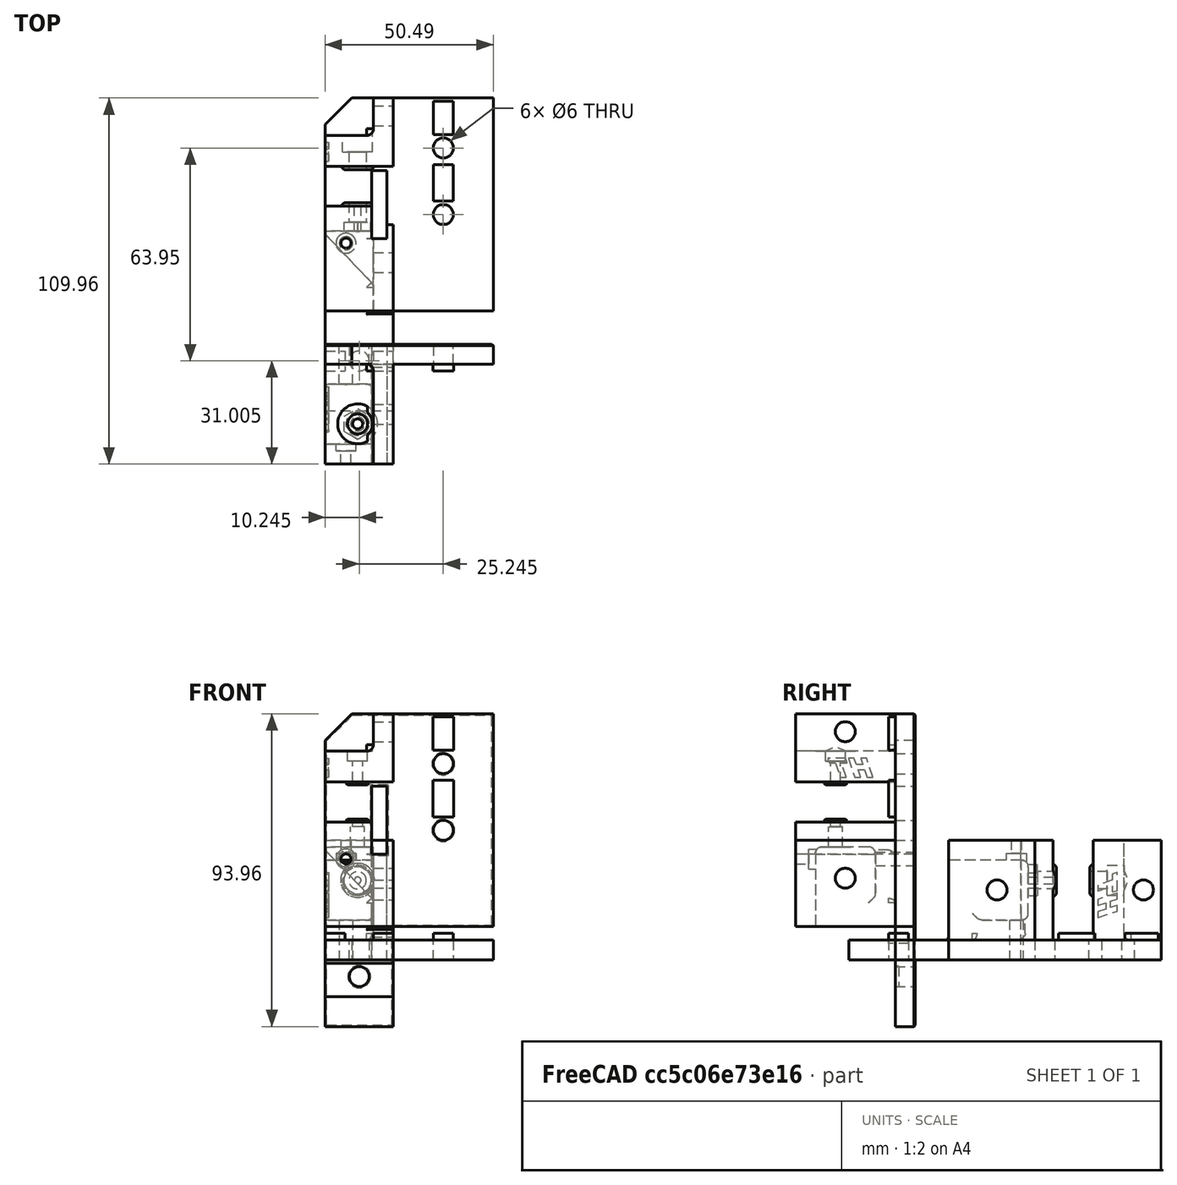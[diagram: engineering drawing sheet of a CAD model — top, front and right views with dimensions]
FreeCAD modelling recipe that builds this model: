
FCSTD DOCUMENT  (FreeCAD 0.18R16146 (Git))
Label: rear-idler-right-2
License: All rights reserved
LicenseURL: http://en.wikipedia.org/wiki/All_rights_reserved
objects: Part::Box×11, Part::Cylinder×11, Part::Cut×10, Part::MultiFuse×7, Part::Feature×5, Part::Chamfer×3
note: 47 computed .brp shape members not serialized (recipe doc carries the construction recipe); baked Part::Feature solids carry a one-line shape summary decoded from their .brp

FEATURE [Part::Feature] Part__Feature  label="PulleyMount_REAR_RIGHT_Body"
  Placement = pos=(-422.5,-448.82,-414) rot=(0,-1,0;1.5708rad)
  shape: bbox 51.93 x 93.95 x 36 mm, 87 faces (baked)
FEATURE [Part::Feature] Part__Feature001  label="PulleyMount_REAR_RIGHT_Body001"
  shape: bbox 51.93 x 93.95 x 36 mm, 87 faces (baked)
FEATURE [Part::Box] Box  label="Cube"
  AttacherType = Attacher::AttachEngine3D
  Height = 3
  Length = 6
  Placement = pos=(12,43,5) rot=(0,0,1;0rad)
  Width = 11
FEATURE [Part::Box] Box001  label="Cube001"
  AttacherType = Attacher::AttachEngine3D
  Height = 3
  Length = 6
  Placement = pos=(12,63,5) rot=(0,0,1;0rad)
  Width = 10
FEATURE [Part::Box] Box002  label="Cube002"
  AttacherType = Attacher::AttachEngine3D
  Height = 3
  Length = 6
  Placement = pos=(-20.49,-8,5) rot=(0,0,1;0rad)
  Width = 6
FEATURE [Part::Box] Box003  label="Cube003"
  AttacherType = Attacher::AttachEngine3D
  Height = 3
  Length = 6
  Placement = pos=(-6,-8,5) rot=(0,0,1;0rad)
  Width = 6
FEATURE [Part::Box] Box004  label="Cube004"
  AttacherType = Attacher::AttachEngine3D
  Height = 3
  Length = 13
  Placement = pos=(-12,4,6.01) rot=(0,0,1;0rad)
  Width = 6
FEATURE [Part::Cut] Cut
  Base = -> Part__Feature001
  Tool = -> Box004
FEATURE [Part::MultiFuse] Fusion
  Shapes = -> [Box003,Box002,Box001,Box,Cut]
FEATURE [Part::Feature] Fusion001
  shape: bbox 51.93 x 93.95 x 36 mm, 110 faces (baked)
FEATURE [Part::Chamfer] Chamfer
  Base = -> Fusion001
  Edges = 15 edges r=0.4: [Edge27,Edge29,Edge30,Edge31,Edge32,Edge33,Edge34,Edge35,Edge36,Edge37,Edge38,Edge39,Edge40,Edge41,Edge42]
FEATURE [Part::Cylinder] Cylinder  label="pos"
  Angle = 360
  AttacherType = Attacher::AttachEngine3D
  Height = 7.5
  Placement = pos=(-10.74,33.96,23.92) rot=(-1,0,0;1.5708rad)
  Radius = 1
FEATURE [Part::Cylinder] Cylinder001  label="pos001"
  Angle = 360
  AttacherType = Attacher::AttachEngine3D
  Height = 7.5
  Placement = pos=(-10.74,33.96,23.92) rot=(-1,0,0;1.5708rad)
  Radius = 6
FEATURE [Part::Box] Box005  label="Cube005"
  AttacherType = Attacher::AttachEngine3D
  Height = 17
  Length = 10
  Placement = pos=(-6.5,33,16) rot=(0,0,1;0rad)
  Width = 23
FEATURE [Part::Cut] Cut001
  Base = -> Cylinder001
  Tool = -> Box005
FEATURE [Part::MultiFuse] Fusion002
  Shapes = -> [Chamfer,Cut001]
FEATURE [Part::Cylinder] Cylinder002  label="pos002"
  Angle = 360
  AttacherType = Attacher::AttachEngine3D
  Height = 9.25
  Placement = pos=(-10.74,53.46,23.92) rot=(-1,0,0;1.5708rad)
  Radius = 6
FEATURE [Part::MultiFuse] Fusion003
  Shapes = -> [Cylinder002,Fusion002]
FEATURE [Part::Cylinder] Cylinder003  label="pos003"
  Angle = 360
  AttacherType = Attacher::AttachEngine3D
  Height = 3
  Placement = pos=(-10.74,50.46,23.92) rot=(-1,0,0;1.5708rad)
  Radius = 6
FEATURE [Part::Cylinder] Cylinder004  label="pos004"
  Angle = 360
  AttacherType = Attacher::AttachEngine3D
  Height = 3
  Placement = pos=(-10.74,41.46,23.92) rot=(-1,0,0;1.5708rad)
  Radius = 6
FEATURE [Part::Cut] Cut002
  Base = -> Fusion003
  Tool = -> Cylinder004
FEATURE [Part::Cut] Cut003
  Base = -> Cut002
  Tool = -> Cylinder003
FEATURE [Part::Cylinder] Cylinder005  label="pos005"
  Angle = 360
  AttacherType = Attacher::AttachEngine3D
  Height = 31.5
  Placement = pos=(-10.74,33.96,23.92) rot=(-1,0,0;1.5708rad)
  Radius = 1.5
FEATURE [Part::Cut] Cut004
  Base = -> Cut003
  Tool = -> Cylinder005
FEATURE [Part::Cylinder] Cylinder006  label="pos006"
  Angle = 360
  AttacherType = Attacher::AttachEngine3D
  Height = 3
  Placement = pos=(-10.74,59.71,23.92) rot=(-1,0,0;1.5708rad)
  Radius = 3
FEATURE [Part::Feature] Body001
  Placement = pos=(-10.74,33.96,23.92) rot=(-1,0,0;1.5708rad)
  shape: bbox 5.543 x 3 x 6.4 mm, 8 faces (baked)
FEATURE [Part::Cylinder] Cylinder007  label="pos007"
  Angle = 360
  AttacherType = Attacher::AttachEngine3D
  Height = 1
  Placement = pos=(-10.74,46.96,23.92) rot=(-1,0,0;1.5708rad)
  Radius = 3.5
FEATURE [Part::Cylinder] Cylinder008  label="pos008"
  Angle = 360
  AttacherType = Attacher::AttachEngine3D
  Height = 1
  Placement = pos=(-10.74,46.96,23.92) rot=(-1,0,0;1.5708rad)
  Radius = 1.5
FEATURE [Part::Cut] Cut007
  Base = -> Cylinder007
  Placement = pos=(0,-5.5,0) rot=(0,0,1;0rad)
  Tool = -> Cylinder008
FEATURE [Part::Feature] Cut007001  label="Cut008"
  Placement = pos=(0,5.5,0) rot=(0,0,1;0rad)
  shape: bbox 7 x 1 x 7 mm, 4 faces (baked)
FEATURE [Part::Chamfer] Chamfer001
  Base = -> Cut007
  Edges = 1 edges r=0.5: [Edge1]
  Placement = pos=(0,-0.1,0) rot=(0,0,1;0rad)
FEATURE [Part::Chamfer] Chamfer002
  Base = -> Cut007001
  Edges = 1 edges r=0.5: [Edge3]
  Placement = pos=(0,0.1,0) rot=(0,0,1;0rad)
FEATURE [Part::Box] Box006  label="Cube006"
  AttacherType = Attacher::AttachEngine3D
  Height = 3
  Length = 6
  Placement = pos=(-20.49,-8.1,5) rot=(0,0,1;0rad)
  Width = 6.2
FEATURE [Part::Box] Box007  label="Cube007"
  AttacherType = Attacher::AttachEngine3D
  Height = 3
  Length = 6
  Placement = pos=(-6,-8.1,5) rot=(0,0,1;0rad)
  Width = 6.2
FEATURE [Part::Box] Box008  label="Cube008"
  AttacherType = Attacher::AttachEngine3D
  Height = 3
  Length = 6.2
  Placement = pos=(11.9,43,5) rot=(0,0,1;0rad)
  Width = 11
FEATURE [Part::Box] Box009  label="Cube009"
  AttacherType = Attacher::AttachEngine3D
  Height = 3
  Length = 6.2
  Placement = pos=(11.9,63,5) rot=(0,0,1;0rad)
  Width = 10
FEATURE [Part::MultiFuse] Fusion005
  Shapes = -> [Box009,Box008,Box007,Box006]
FEATURE [Part::Cylinder] Cylinder009  label="pos009"
  Angle = 360
  AttacherType = Attacher::AttachEngine3D
  Height = 6
  Placement = pos=(-10.74,33.96,23.92) rot=(-1,0,0;1.5708rad)
  Radius = 2.1
FEATURE [Part::Cylinder] Cylinder010  label="pos010"
  Angle = 360
  AttacherType = Attacher::AttachEngine3D
  Height = 6
  Placement = pos=(-10.74,33.96,23.92) rot=(-1,0,0;1.5708rad)
  Radius = 3.5
FEATURE [Part::Cut] Cut005
  Base = -> Cut004
  Tool = -> Cylinder006
FEATURE [Part::Cut] Cut006
  Base = -> Cut005
  Tool = -> Body001
FEATURE [Part::MultiFuse] Fusion004
  Shapes = -> [Cut006,Chamfer002,Chamfer001]
FEATURE [Part::MultiFuse] Fusion006
  Shapes = -> [Fusion005,Fusion004]
FEATURE [Part::MultiFuse] Fusion007
  Shapes = -> [Fusion006,Cylinder010]
FEATURE [Part::Cut] Cut007002
  Base = -> Fusion007
  Placement = pos=(0,0,0) rot=(1,0,0;1.5708rad)
  Tool = -> Cylinder009
FEATURE [Part::Box] Box010  label="Cube010"
  AttacherType = Attacher::AttachEngine3D
  Height = 10
  Length = 30
  Placement = pos=(-24,-16,-11) rot=(0,0,1;0rad)
  Width = 10
FEATURE [Part::Cut] Cut007003
  Base = -> Cut007002
  Tool = -> Box010
